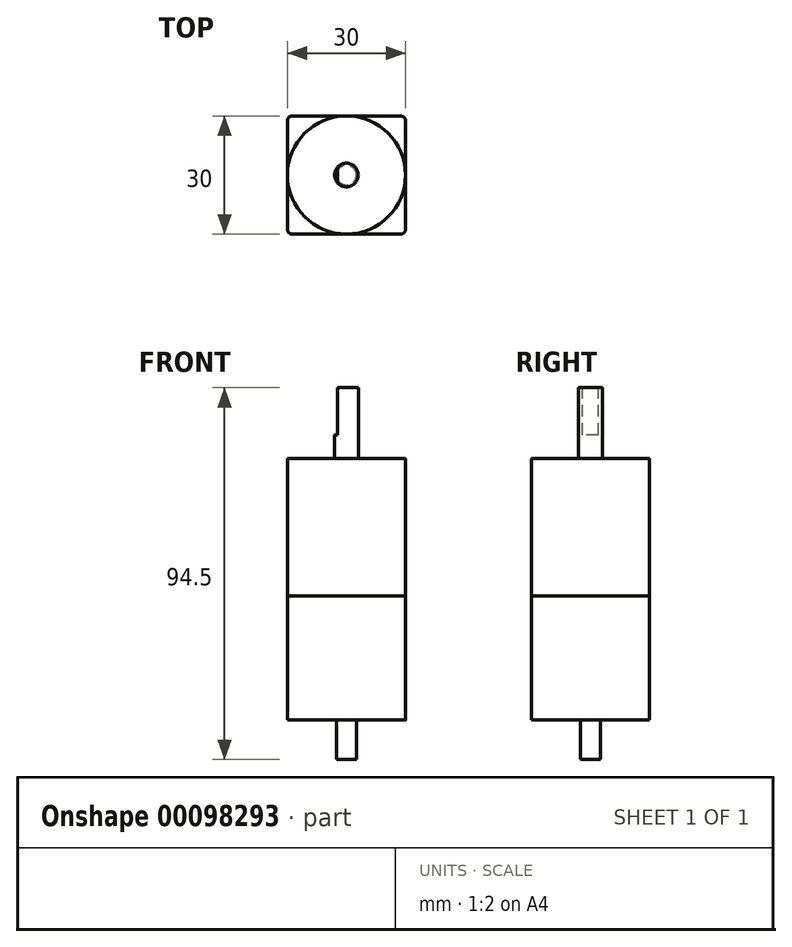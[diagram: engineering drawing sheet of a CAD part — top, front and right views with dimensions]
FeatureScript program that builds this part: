
annotation { "Feature Type Name" : "Feature", "Feature Type Description" : "" }
export const myFeature = defineFeature(function(context is Context, id is Id, definition is map)
    precondition{}
    {
        {
            assignVariable(context, id + "F0", {"name" : "MotorL", "anyValue" : 31.5});
        }
        {
            assignVariable(context, id + "F1", {"name" : "GearboxL", "anyValue" : 35});
        }
        {
            assignVariable(context, id + "F2", {"name" : "FrontShaftL", "anyValue" : 18});
        }
        {
            assignVariable(context, id + "F3", {"name" : "FrontShaftDCutL", "anyValue" : 12});
        }
        {
            assignVariable(context, id + "F4", {"name" : "RearShaftL", "anyValue" : 10});
        }
        {
            var Q0;
            Q0=qCreatedBy(makeId("Top.planeOp"),FACE);
            var sketch = newSketch(context, id + "F5", { "sketchPlane" : qUnion([Q0])});
            skLineSegment(sketch, "E0.bottom", {"start": v(-15, 15) * mm, "end": v(15, 15) * mm});
            skLineSegment(sketch, "E0.top", {"start": v(-15, -15) * mm, "end": v(15, -15) * mm});
            skLineSegment(sketch, "E0.left", {"start": v(-15, 15) * mm, "end": v(-15, -15) * mm});
            skLineSegment(sketch, "E0.right", {"start": v(15, 15) * mm, "end": v(15, -15) * mm});
            skSolve(sketch);
        }
        {
            var Q0;
            Q0=makeQuery(id+"F5.imprint","IMPRINT",FACE,{"disambiguationData":[TD([[makeQuery(id+"F5.imprint","IMPRINT",EDGE,{"derivedFrom":sQuery(id+"F5.wireOp",EDGE,"E0.bottom")}),-1.0]])]});
            extrude(context, id + "F6", {"entities" : qUnion([Q0]), "depth" : (getVariable(context, 'MotorL')) * mm});
        }
        {
            var Q0;
            Q0=makeQuery(id+"F6.opExtrude","CAP_FACE",FACE,{"disambiguationData":[OSD([sQuery(id+"F5.wireOp",EDGE,"E0.bottom"),sQuery(id+"F5.wireOp",EDGE,"E0.top"),sQuery(id+"F5.wireOp",EDGE,"E0.left"),sQuery(id+"F5.wireOp",EDGE,"E0.right")])],"isStart":false});
            var sketch = newSketch(context, id + "F7", { "sketchPlane" : qUnion([Q0])});
            skCircle(sketch, "E1", {"center": v(0, 0) * mm, "radius": 15 * mm});
            skSolve(sketch);
        }
        {
            var Q0;
            Q0 = qSketchRegion(id + "F7", true);
            extrude(context, id + "F8", {"entities" : qUnion([Q0]), "depth" : (getVariable(context, 'GearboxL')) * mm});
        }
        {
            var Q0;
            Q0=makeQuery(id+"F8.opExtrude","CAP_FACE",FACE,{"disambiguationData":[OSD([sQuery(id+"F7.wireOp",EDGE,"E1")])],"isStart":false});
            var sketch = newSketch(context, id + "F9", { "sketchPlane" : qUnion([Q0])});
            skCircle(sketch, "E2", {"center": v(0, 0) * mm, "radius": 3 * mm});
            skSolve(sketch);
        }
        {
            var Q0;
            Q0 = qSketchRegion(id + "F9", true);
            extrude(context, id + "F10", {"entities" : qUnion([Q0]), "operationType" : NewBodyOperationType.ADD, "depth" : (getVariable(context, 'FrontShaftL')) * mm});
        }
        {
            var Q0;
            Q0=makeQuery(id+"F10.opExtrude","CAP_FACE",FACE,{"disambiguationData":[OSD([sQuery(id+"F9.wireOp",EDGE,"E2")])],"isStart":false});
            var sketch = newSketch(context, id + "F11", { "sketchPlane" : qUnion([Q0])});
            skLineSegment(sketch, "E3", {"start": v(-2.25, 1.98) * mm, "end": v(-2.25, -1.98) * mm});
            skSolve(sketch);
        }
        {
            var Q0;
            {var subQ0=sQuery(id+"F11.wireOp",EDGE,"E3");Q0=makeQuery(id+"F11.imprint","IMPRINT",FACE,{"disambiguationData":[TD([[makeQuery(id+"F11.imprint","IMPRINT",EDGE,{"derivedFrom":subQ0}),-1.0]])]});}
            extrude(context, id + "F12", {"entities" : qUnion([Q0]), "operationType" : NewBodyOperationType.REMOVE, "oppositeDirection" : true, "depth" : (getVariable(context, 'FrontShaftDCutL')) * mm});
        }
        {
            var Q0;
            Q0=makeQuery(id+"F6.opExtrude","CAP_FACE",FACE,{"disambiguationData":[OSD([sQuery(id+"F5.wireOp",EDGE,"E0.bottom"),sQuery(id+"F5.wireOp",EDGE,"E0.top"),sQuery(id+"F5.wireOp",EDGE,"E0.left"),sQuery(id+"F5.wireOp",EDGE,"E0.right")])],"isStart":true});
            var sketch = newSketch(context, id + "F13", { "sketchPlane" : qUnion([Q0])});
            skCircle(sketch, "E4", {"center": v(0, 0) * mm, "radius": 2.5 * mm});
            skSolve(sketch);
        }
        {
            var Q0;
            Q0 = qSketchRegion(id + "F13", true);
            extrude(context, id + "F14", {"entities" : qUnion([Q0]), "operationType" : NewBodyOperationType.ADD, "depth" : (getVariable(context, 'RearShaftL')) * mm});
        }
        {
            var Q0;
            Q0=makeQuery(id+"F6.opExtrude","SWEPT_EDGE",EDGE,{"disambiguationData":[OSD([sQuery(id+"F5.wireOp",EDGE,"E0.top"),sQuery(id+"F5.wireOp",EDGE,"E0.left")])]});
            var Q1;
            Q1=makeQuery(id+"F6.opExtrude","SWEPT_EDGE",EDGE,{"disambiguationData":[OSD([sQuery(id+"F5.wireOp",EDGE,"E0.top"),sQuery(id+"F5.wireOp",EDGE,"E0.right")])]});
            var Q2;
            Q2=makeQuery(id+"F6.opExtrude","SWEPT_EDGE",EDGE,{"disambiguationData":[OSD([sQuery(id+"F5.wireOp",EDGE,"E0.bottom"),sQuery(id+"F5.wireOp",EDGE,"E0.right")])]});
            var Q3;
            Q3=makeQuery(id+"F6.opExtrude","SWEPT_EDGE",EDGE,{"disambiguationData":[OSD([sQuery(id+"F5.wireOp",EDGE,"E0.bottom"),sQuery(id+"F5.wireOp",EDGE,"E0.left")])]});
            fillet(context, id + "F15", {"entities" : qUnion([Q0, Q1, Q2, Q3]), "radius" : 1.2 * mm, "tangentPropagation" : true, "allowEdgeOverflow" : false});
        }
    });
